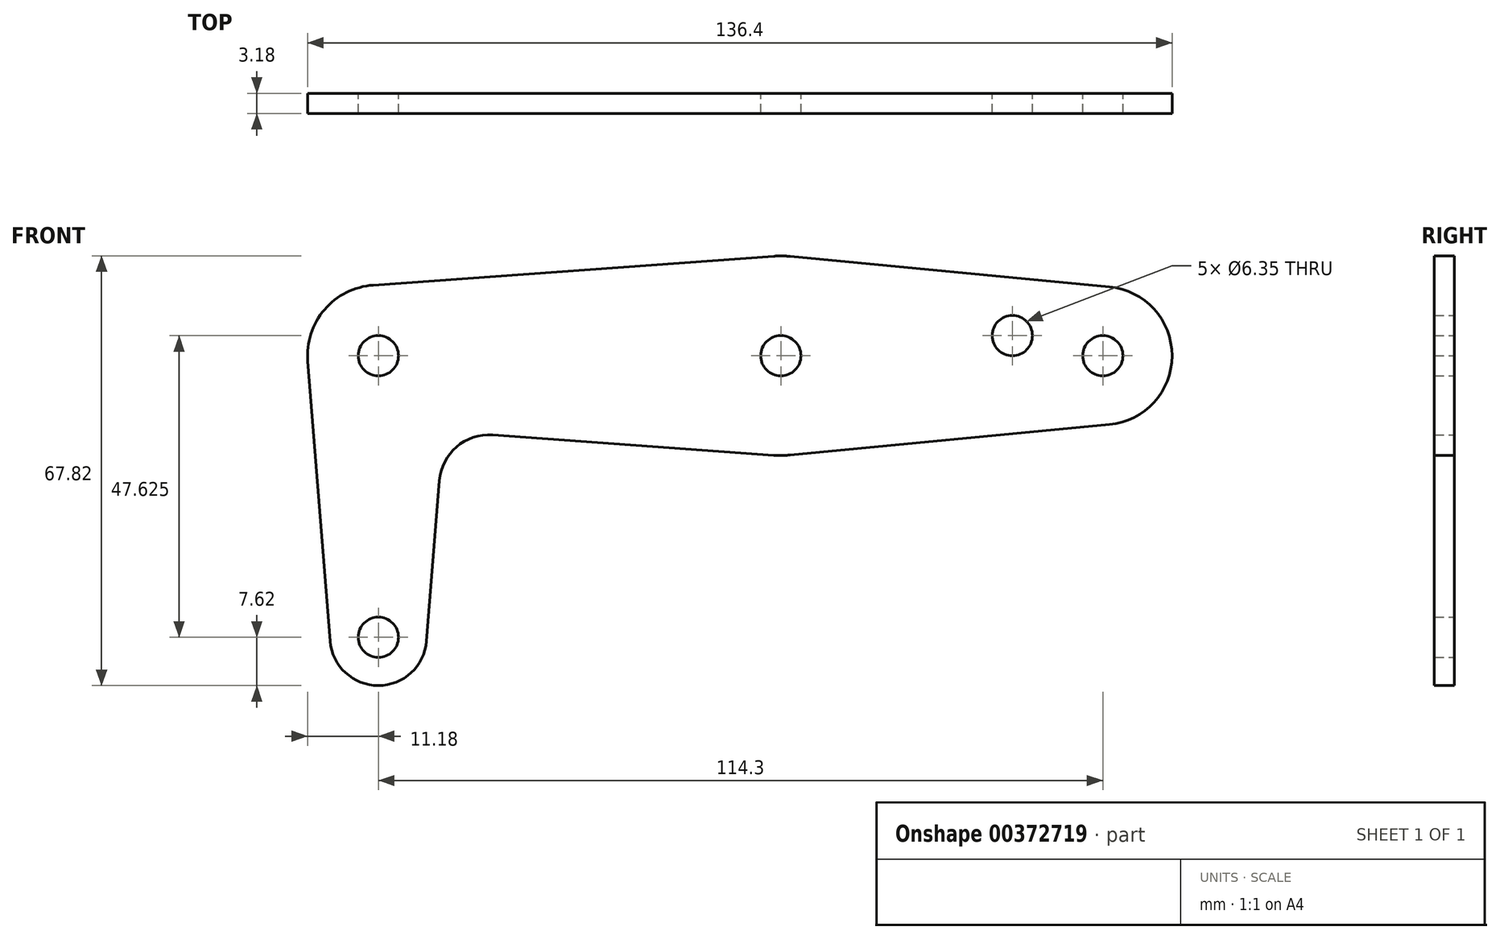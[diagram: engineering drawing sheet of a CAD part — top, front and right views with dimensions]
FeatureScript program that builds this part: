
annotation { "Feature Type Name" : "Feature", "Feature Type Description" : "" }
export const myFeature = defineFeature(function(context is Context, id is Id, definition is map)
    precondition{}
    {
        {
            var Q0;
            Q0=qCreatedBy(makeId("Front.planeOp"),FACE);
            var sketch = newSketch(context, id + "F0", { "sketchPlane" : qUnion([Q0])});
            skCircle(sketch, "E0", {"center": v(-63.5, 0) * mm, "radius": 3.18 * mm});
            skCircle(sketch, "E1", {"center": v(0, 0) * mm, "radius": 3.18 * mm});
            skCircle(sketch, "E2", {"center": v(50.8, 0) * mm, "radius": 3.18 * mm});
            skCircle(sketch, "E3", {"center": v(36.53, 3.17) * mm, "radius": 3.18 * mm});
            skCircle(sketch, "E4", {"center": v(-63.5, -44.45) * mm, "radius": 3.18 * mm});
            skArc(sketch, "E5", {"start": v(-71.1, -45.06) * mm, "mid": v(-63.5, -52.07) * mm, "end": v(-55.9, -45.06) * mm});
            skArc(sketch, "E6", {"start": v(-64.3, 11.15) * mm, "mid": v(-71.98, 7.28) * mm, "end": v(-74.64, -0.9) * mm});
            skArc(sketch, "E7", {"start": v(1.5, 15.68) * mm, "mid": v(0.18, 15.75) * mm, "end": v(-1.13, 15.7) * mm});
            skArc(sketch, "E8", {"start": v(51.84, -10.87) * mm, "mid": v(61.72, 0) * mm, "end": v(51.84, 10.87) * mm});
            skLineSegment(sketch, "E9", {"start": v(-71.1, -45.06) * mm, "end": v(-74.64, -0.9) * mm});
            skLineSegment(sketch, "E10", {"start": v(-55.9, -45.06) * mm, "end": v(-53.87, -19.73) * mm});
            skLineSegment(sketch, "E11", {"start": v(-45.46, -12.5) * mm, "end": v(-1.13, -15.7) * mm});
            skLineSegment(sketch, "E12", {"start": v(-64.3, 11.15) * mm, "end": v(-1.13, 15.7) * mm});
            skLineSegment(sketch, "E13", {"start": v(1.5, -15.68) * mm, "end": v(51.84, -10.87) * mm});
            skLineSegment(sketch, "E14", {"start": v(1.5, 15.68) * mm, "end": v(51.84, 10.87) * mm});
            skPoint(sketch, "E15.orphan", {"position": v(-52.29, 0) * mm});
            skArc(sketch, "E16.trimOffspring", {"start": v(-1.13, -15.7) * mm, "mid": v(0.18, -15.75) * mm, "end": v(1.5, -15.68) * mm});
            skPoint(sketch, "E17.visualSharp", {"position": v(-53.25, -11.95) * mm});
            skArc(sketch, "E17.filletArc", {"start": v(-45.46, -12.5) * mm, "mid": v(-51.15, -14.39) * mm, "end": v(-53.87, -19.73) * mm});
            skSolve(sketch);
        }
        {
            var Q0;
            Q0 = qSketchRegion(id + "F0", true);
            extrude(context, id + "F1", {"entities" : qUnion([Q0]), "endBound" : BoundingType.SYMMETRIC, "depth" : 3.17 * mm});
        }
    });
